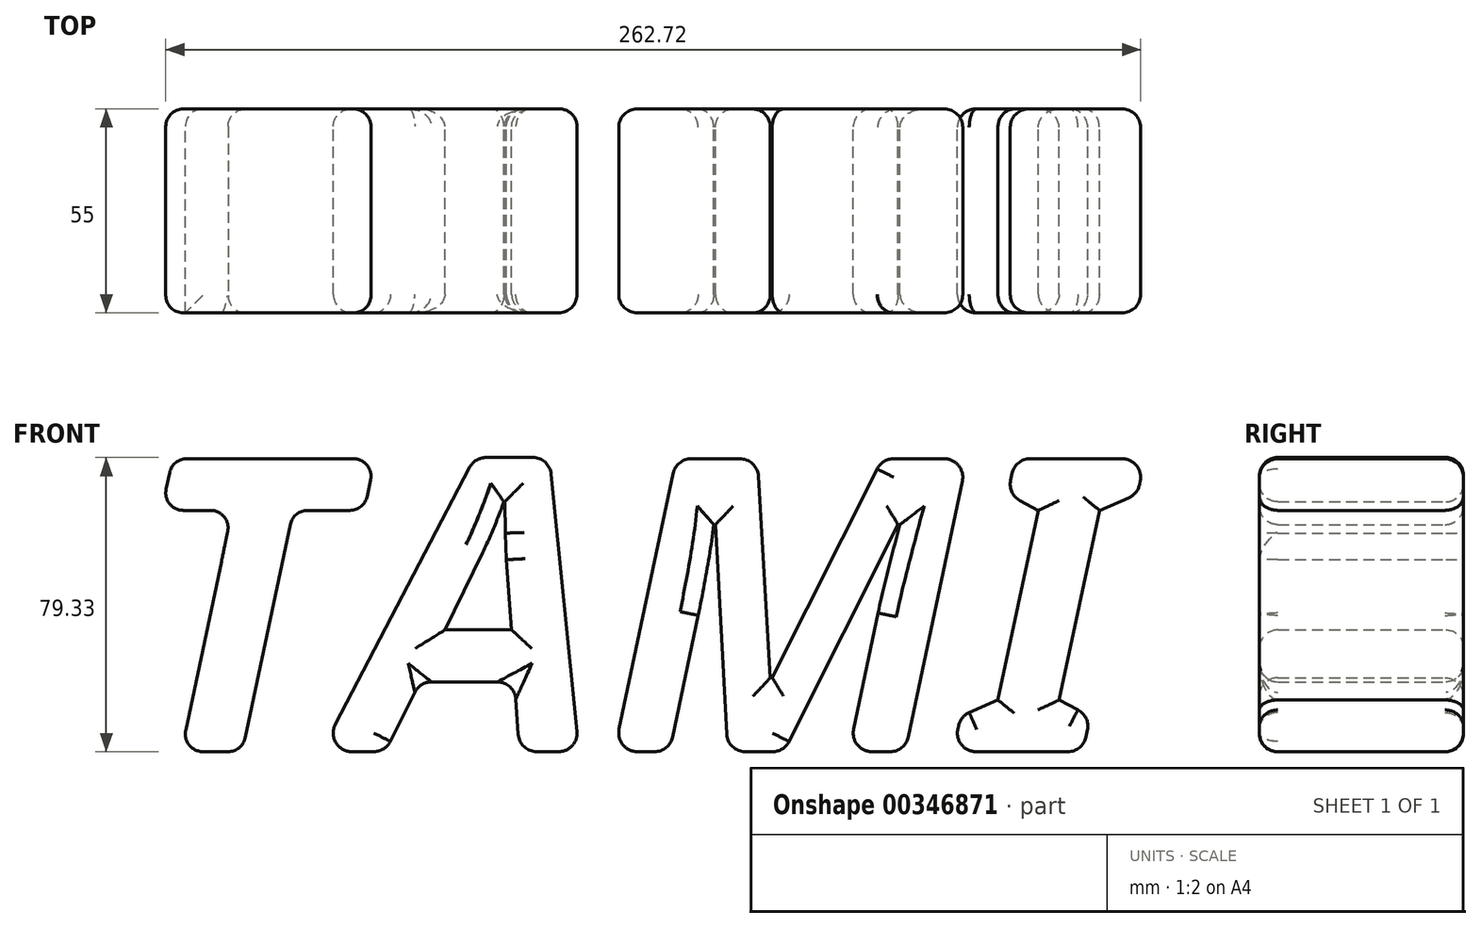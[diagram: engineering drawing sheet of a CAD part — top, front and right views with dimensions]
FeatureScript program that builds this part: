
annotation { "Feature Type Name" : "Feature", "Feature Type Description" : "" }
export const myFeature = defineFeature(function(context is Context, id is Id, definition is map)
    precondition{}
    {
        {
            var Q0;
            Q0=qCreatedBy(makeId("Front.planeOp"),FACE);
            var sketch = newSketch(context, id + "F0", { "sketchPlane" : qUnion([Q0])});
            skText(sketch, "E0", { "text": "TAMI", "fontName": "NotoSans-BoldItalic.ttf"});
            const initialGuessF0  = {"E0": [0, 0, 1, 0, 0.07968]};
            skSetInitialGuess(sketch, initialGuessF0);
            skSolve(sketch);
        }
        {
            var Q0;
            Q0 = qSketchRegion(id + "F0", true);
            extrude(context, id + "F1", {"entities" : qUnion([Q0]), "depth" : 30 * mm, "hasSecondDirection" : true, "secondDirectionOppositeDirection" : true, "secondDirectionDepth" : 25 * mm});
        }
        {
            var Q0;
            Q0=makeQuery(id+"F1.opExtrude","CAP_FACE",FACE,{"disambiguationData":[OSD([sQuery(id+"F0.wireOp",EDGE,"E0.sketch_text.stroke-8"),sQuery(id+"F0.wireOp",EDGE,"E0.sketch_text.stroke-9"),sQuery(id+"F0.wireOp",EDGE,"E0.sketch_text.stroke-10"),sQuery(id+"F0.wireOp",EDGE,"E0.sketch_text.stroke-11"),sQuery(id+"F0.wireOp",EDGE,"E0.sketch_text.stroke-12"),sQuery(id+"F0.wireOp",EDGE,"E0.sketch_text.stroke-13"),sQuery(id+"F0.wireOp",EDGE,"E0.sketch_text.stroke-14"),sQuery(id+"F0.wireOp",EDGE,"E0.sketch_text.stroke-15"),sQuery(id+"F0.wireOp",EDGE,"E0.sketch_text.stroke-16"),sQuery(id+"F0.wireOp",EDGE,"E0.sketch_text.stroke-17"),sQuery(id+"F0.wireOp",EDGE,"E0.sketch_text.stroke-18"),sQuery(id+"F0.wireOp",EDGE,"E0.sketch_text.stroke-19"),sQuery(id+"F0.wireOp",EDGE,"E0.sketch_text.stroke-20"),sQuery(id+"F0.wireOp",EDGE,"E0.sketch_text.stroke-21"),sQuery(id+"F0.wireOp",EDGE,"E0.sketch_text.stroke-22")])],"isStart":true});
            var Q1;
            Q1=makeQuery(id+"F1.opExtrude","CAP_EDGE",EDGE,{"disambiguationData":[OSD([sQuery(id+"F0.wireOp",EDGE,"E0.sketch_text.stroke-4")])],"isStart":true});
            var Q2;
            Q2=makeQuery(id+"F1.opExtrude","CAP_EDGE",EDGE,{"disambiguationData":[OSD([sQuery(id+"F0.wireOp",EDGE,"E0.sketch_text.stroke-7")])],"isStart":true});
            var Q3;
            Q3=makeQuery(id+"F1.opExtrude","CAP_EDGE",EDGE,{"disambiguationData":[OSD([sQuery(id+"F0.wireOp",EDGE,"E0.sketch_text.stroke-0")])],"isStart":true});
            var Q4;
            Q4=makeQuery(id+"F1.opExtrude","CAP_EDGE",EDGE,{"disambiguationData":[OSD([sQuery(id+"F0.wireOp",EDGE,"E0.sketch_text.stroke-6")])],"isStart":true});
            var Q5;
            Q5=makeQuery(id+"F1.opExtrude","CAP_EDGE",EDGE,{"disambiguationData":[OSD([sQuery(id+"F0.wireOp",EDGE,"E0.sketch_text.stroke-5")])],"isStart":true});
            var Q6;
            Q6=makeQuery(id+"F1.opExtrude","SWEPT_EDGE",EDGE,{"disambiguationData":[OSD([sQuery(id+"F0.wireOp",EDGE,"E0.sketch_text.stroke-4"),sQuery(id+"F0.wireOp",EDGE,"E0.sketch_text.stroke-5")])]});
            var Q7;
            Q7=makeQuery(id+"F1.opExtrude","CAP_EDGE",EDGE,{"disambiguationData":[OSD([sQuery(id+"F0.wireOp",EDGE,"E0.sketch_text.stroke-3")])],"isStart":true});
            var Q8;
            Q8=makeQuery(id+"F1.opExtrude","CAP_EDGE",EDGE,{"disambiguationData":[OSD([sQuery(id+"F0.wireOp",EDGE,"E0.sketch_text.stroke-2")])],"isStart":true});
            var Q9;
            Q9=makeQuery(id+"F1.opExtrude","CAP_EDGE",EDGE,{"disambiguationData":[OSD([sQuery(id+"F0.wireOp",EDGE,"E0.sketch_text.stroke-4")])],"isStart":false});
            var Q10;
            Q10=makeQuery(id+"F1.opExtrude","CAP_EDGE",EDGE,{"disambiguationData":[OSD([sQuery(id+"F0.wireOp",EDGE,"E0.sketch_text.stroke-5")])],"isStart":false});
            var Q11;
            Q11=makeQuery(id+"F1.opExtrude","CAP_EDGE",EDGE,{"disambiguationData":[OSD([sQuery(id+"F0.wireOp",EDGE,"E0.sketch_text.stroke-6")])],"isStart":false});
            var Q12;
            Q12=makeQuery(id+"F1.opExtrude","CAP_EDGE",EDGE,{"disambiguationData":[OSD([sQuery(id+"F0.wireOp",EDGE,"E0.sketch_text.stroke-2")])],"isStart":false});
            var Q13;
            Q13=makeQuery(id+"F1.opExtrude","CAP_EDGE",EDGE,{"disambiguationData":[OSD([sQuery(id+"F0.wireOp",EDGE,"E0.sketch_text.stroke-3")])],"isStart":false});
            var Q14;
            Q14=makeQuery(id+"F1.opExtrude","SWEPT_EDGE",EDGE,{"disambiguationData":[OSD([sQuery(id+"F0.wireOp",EDGE,"E0.sketch_text.stroke-3"),sQuery(id+"F0.wireOp",EDGE,"E0.sketch_text.stroke-4")])]});
            var Q15;
            Q15=makeQuery(id+"F1.opExtrude","CAP_EDGE",EDGE,{"disambiguationData":[OSD([sQuery(id+"F0.wireOp",EDGE,"E0.sketch_text.stroke-1")])],"isStart":true});
            var Q16;
            Q16=makeQuery(id+"F1.opExtrude","SWEPT_EDGE",EDGE,{"disambiguationData":[OSD([sQuery(id+"F0.wireOp",EDGE,"E0.sketch_text.stroke-2"),sQuery(id+"F0.wireOp",EDGE,"E0.sketch_text.stroke-3")])]});
            var Q17;
            Q17=makeQuery(id+"F1.opExtrude","SWEPT_EDGE",EDGE,{"disambiguationData":[OSD([sQuery(id+"F0.wireOp",EDGE,"E0.sketch_text.stroke-1"),sQuery(id+"F0.wireOp",EDGE,"E0.sketch_text.stroke-2")])]});
            var Q18;
            Q18=makeQuery(id+"F1.opExtrude","SWEPT_EDGE",EDGE,{"disambiguationData":[OSD([sQuery(id+"F0.wireOp",EDGE,"E0.sketch_text.stroke-0"),sQuery(id+"F0.wireOp",EDGE,"E0.sketch_text.stroke-7")])]});
            var Q19;
            Q19=makeQuery(id+"F1.opExtrude","SWEPT_EDGE",EDGE,{"disambiguationData":[OSD([sQuery(id+"F0.wireOp",EDGE,"E0.sketch_text.stroke-0"),sQuery(id+"F0.wireOp",EDGE,"E0.sketch_text.stroke-1")])]});
            var Q20;
            Q20=makeQuery(id+"F1.opExtrude","CAP_EDGE",EDGE,{"disambiguationData":[OSD([sQuery(id+"F0.wireOp",EDGE,"E0.sketch_text.stroke-0")])],"isStart":false});
            var Q21;
            Q21=makeQuery(id+"F1.opExtrude","CAP_EDGE",EDGE,{"disambiguationData":[OSD([sQuery(id+"F0.wireOp",EDGE,"E0.sketch_text.stroke-7")])],"isStart":false});
            var Q22;
            Q22=makeQuery(id+"F1.opExtrude","SWEPT_FACE",FACE,{"disambiguationData":[OSD([sQuery(id+"F0.wireOp",EDGE,"E0.sketch_text.stroke-6")])]});
            fillet(context, id + "F2", {"entities" : qUnion([Q0, Q1, Q2, Q3, Q4, Q5, Q6, Q7, Q8, Q9, Q10, Q11, Q12, Q13, Q14, Q15, Q16, Q17, Q18, Q19, Q20, Q21, Q22]), "radius" : 4.74 * mm, "tangentPropagation" : true, "allowEdgeOverflow" : false});
        }
        {
            var Q0;
            Q0=makeQuery(id+"F1.opExtrude","SWEPT_EDGE",EDGE,{"disambiguationData":[OSD([sQuery(id+"F0.wireOp",EDGE,"E0.sketch_text.stroke-12"),sQuery(id+"F0.wireOp",EDGE,"E0.sketch_text.stroke-13")])]});
            var Q1;
            Q1=makeQuery(id+"F1.opExtrude","SWEPT_FACE",FACE,{"disambiguationData":[OSD([sQuery(id+"F0.wireOp",EDGE,"E0.sketch_text.stroke-12")])]});
            var Q2;
            Q2=makeQuery(id+"F1.opExtrude","SWEPT_FACE",FACE,{"disambiguationData":[OSD([sQuery(id+"F0.wireOp",EDGE,"E0.sketch_text.stroke-11")])]});
            var Q3;
            Q3=makeQuery(id+"F1.opExtrude","CAP_EDGE",EDGE,{"disambiguationData":[OSD([sQuery(id+"F0.wireOp",EDGE,"E0.sketch_text.stroke-16")])],"isStart":false});
            var Q4;
            Q4=makeQuery(id+"F1.opExtrude","CAP_FACE",FACE,{"disambiguationData":[OSD([sQuery(id+"F0.wireOp",EDGE,"E0.sketch_text.stroke-8"),sQuery(id+"F0.wireOp",EDGE,"E0.sketch_text.stroke-9"),sQuery(id+"F0.wireOp",EDGE,"E0.sketch_text.stroke-10"),sQuery(id+"F0.wireOp",EDGE,"E0.sketch_text.stroke-11"),sQuery(id+"F0.wireOp",EDGE,"E0.sketch_text.stroke-12"),sQuery(id+"F0.wireOp",EDGE,"E0.sketch_text.stroke-13"),sQuery(id+"F0.wireOp",EDGE,"E0.sketch_text.stroke-14"),sQuery(id+"F0.wireOp",EDGE,"E0.sketch_text.stroke-15"),sQuery(id+"F0.wireOp",EDGE,"E0.sketch_text.stroke-16"),sQuery(id+"F0.wireOp",EDGE,"E0.sketch_text.stroke-17"),sQuery(id+"F0.wireOp",EDGE,"E0.sketch_text.stroke-18"),sQuery(id+"F0.wireOp",EDGE,"E0.sketch_text.stroke-19"),sQuery(id+"F0.wireOp",EDGE,"E0.sketch_text.stroke-20"),sQuery(id+"F0.wireOp",EDGE,"E0.sketch_text.stroke-21"),sQuery(id+"F0.wireOp",EDGE,"E0.sketch_text.stroke-22")])],"isStart":false});
            var Q5;
            Q5=makeQuery(id+"F1.opExtrude","SWEPT_FACE",FACE,{"disambiguationData":[OSD([sQuery(id+"F0.wireOp",EDGE,"E0.sketch_text.stroke-13")])]});
            fillet(context, id + "F3", {"entities" : qUnion([Q0, Q1, Q2, Q3, Q4, Q5]), "radius" : 5 * mm, "tangentPropagation" : true, "allowEdgeOverflow" : false});
        }
        {
            var Q0;
            Q0=makeQuery(id+"F1.opExtrude","SWEPT_EDGE",EDGE,{"disambiguationData":[OSD([sQuery(id+"F0.wireOp",EDGE,"E0.sketch_text.stroke-8"),sQuery(id+"F0.wireOp",EDGE,"E0.sketch_text.stroke-15")])]});
            var Q1;
            Q1=makeQuery(id+"F1.opExtrude","SWEPT_FACE",FACE,{"disambiguationData":[OSD([sQuery(id+"F0.wireOp",EDGE,"E0.sketch_text.stroke-14")])]});
            var Q2;
            Q2=makeQuery(id+"F1.opExtrude","SWEPT_EDGE",EDGE,{"disambiguationData":[OSD([sQuery(id+"F0.wireOp",EDGE,"E0.sketch_text.stroke-8"),sQuery(id+"F0.wireOp",EDGE,"E0.sketch_text.stroke-9")])]});
            var Q3;
            Q3=makeQuery(id+"F1.opExtrude","SWEPT_EDGE",EDGE,{"disambiguationData":[OSD([sQuery(id+"F0.wireOp",EDGE,"E0.sketch_text.stroke-9"),sQuery(id+"F0.wireOp",EDGE,"E0.sketch_text.stroke-10")])]});
            var Q4;
            Q4=makeQuery(id+"F1.opExtrude","SWEPT_FACE",FACE,{"disambiguationData":[OSD([sQuery(id+"F0.wireOp",EDGE,"E0.sketch_text.stroke-36")])]});
            var Q5;
            Q5=makeQuery(id+"F1.opExtrude","CAP_FACE",FACE,{"disambiguationData":[OSD([sQuery(id+"F0.wireOp",EDGE,"E0.sketch_text.stroke-23"),sQuery(id+"F0.wireOp",EDGE,"E0.sketch_text.stroke-24"),sQuery(id+"F0.wireOp",EDGE,"E0.sketch_text.stroke-25"),sQuery(id+"F0.wireOp",EDGE,"E0.sketch_text.stroke-26"),sQuery(id+"F0.wireOp",EDGE,"E0.sketch_text.stroke-27"),sQuery(id+"F0.wireOp",EDGE,"E0.sketch_text.stroke-28"),sQuery(id+"F0.wireOp",EDGE,"E0.sketch_text.stroke-29"),sQuery(id+"F0.wireOp",EDGE,"E0.sketch_text.stroke-30"),sQuery(id+"F0.wireOp",EDGE,"E0.sketch_text.stroke-31"),sQuery(id+"F0.wireOp",EDGE,"E0.sketch_text.stroke-32"),sQuery(id+"F0.wireOp",EDGE,"E0.sketch_text.stroke-33"),sQuery(id+"F0.wireOp",EDGE,"E0.sketch_text.stroke-34"),sQuery(id+"F0.wireOp",EDGE,"E0.sketch_text.stroke-35"),sQuery(id+"F0.wireOp",EDGE,"E0.sketch_text.stroke-36"),sQuery(id+"F0.wireOp",EDGE,"E0.sketch_text.stroke-37"),sQuery(id+"F0.wireOp",EDGE,"E0.sketch_text.stroke-38"),sQuery(id+"F0.wireOp",EDGE,"E0.sketch_text.stroke-39"),sQuery(id+"F0.wireOp",EDGE,"E0.sketch_text.stroke-40")])],"isStart":false});
            fillet(context, id + "F4", {"entities" : qUnion([Q0, Q1, Q2, Q3, Q4, Q5]), "radius" : 5 * mm, "tangentPropagation" : true, "allowEdgeOverflow" : false});
        }
        {
            var Q0;
            Q0=makeQuery(id+"F1.opExtrude","CAP_FACE",FACE,{"disambiguationData":[OSD([sQuery(id+"F0.wireOp",EDGE,"E0.sketch_text.stroke-23"),sQuery(id+"F0.wireOp",EDGE,"E0.sketch_text.stroke-24"),sQuery(id+"F0.wireOp",EDGE,"E0.sketch_text.stroke-25"),sQuery(id+"F0.wireOp",EDGE,"E0.sketch_text.stroke-26"),sQuery(id+"F0.wireOp",EDGE,"E0.sketch_text.stroke-27"),sQuery(id+"F0.wireOp",EDGE,"E0.sketch_text.stroke-28"),sQuery(id+"F0.wireOp",EDGE,"E0.sketch_text.stroke-29"),sQuery(id+"F0.wireOp",EDGE,"E0.sketch_text.stroke-30"),sQuery(id+"F0.wireOp",EDGE,"E0.sketch_text.stroke-31"),sQuery(id+"F0.wireOp",EDGE,"E0.sketch_text.stroke-32"),sQuery(id+"F0.wireOp",EDGE,"E0.sketch_text.stroke-33"),sQuery(id+"F0.wireOp",EDGE,"E0.sketch_text.stroke-34"),sQuery(id+"F0.wireOp",EDGE,"E0.sketch_text.stroke-35"),sQuery(id+"F0.wireOp",EDGE,"E0.sketch_text.stroke-36"),sQuery(id+"F0.wireOp",EDGE,"E0.sketch_text.stroke-37"),sQuery(id+"F0.wireOp",EDGE,"E0.sketch_text.stroke-38"),sQuery(id+"F0.wireOp",EDGE,"E0.sketch_text.stroke-39"),sQuery(id+"F0.wireOp",EDGE,"E0.sketch_text.stroke-40")])],"isStart":true});
            var Q1;
            Q1=makeQuery(id+"F1.opExtrude","SWEPT_FACE",FACE,{"disambiguationData":[OSD([sQuery(id+"F0.wireOp",EDGE,"E0.sketch_text.stroke-38")])]});
            var Q2;
            Q2=makeQuery(id+"F1.opExtrude","SWEPT_FACE",FACE,{"disambiguationData":[OSD([sQuery(id+"F0.wireOp",EDGE,"E0.sketch_text.stroke-24")])]});
            var Q3;
            Q3=makeQuery(id+"F1.opExtrude","SWEPT_EDGE",EDGE,{"disambiguationData":[OSD([sQuery(id+"F0.wireOp",EDGE,"E0.sketch_text.stroke-26"),sQuery(id+"F0.wireOp",EDGE,"E0.sketch_text.stroke-27")])]});
            var Q4;
            Q4=makeQuery(id+"F1.opExtrude","SWEPT_EDGE",EDGE,{"disambiguationData":[OSD([sQuery(id+"F0.wireOp",EDGE,"E0.sketch_text.stroke-31"),sQuery(id+"F0.wireOp",EDGE,"E0.sketch_text.stroke-32")])]});
            var Q5;
            Q5=makeQuery(id+"F1.opExtrude","SWEPT_EDGE",EDGE,{"disambiguationData":[OSD([sQuery(id+"F0.wireOp",EDGE,"E0.sketch_text.stroke-30"),sQuery(id+"F0.wireOp",EDGE,"E0.sketch_text.stroke-31")])]});
            fillet(context, id + "F5", {"entities" : qUnion([Q0, Q1, Q2, Q3, Q4, Q5]), "radius" : 5 * mm, "tangentPropagation" : true, "allowEdgeOverflow" : false});
        }
        {
            var Q0;
            Q0=makeQuery(id+"F1.opExtrude","SWEPT_EDGE",EDGE,{"disambiguationData":[OSD([sQuery(id+"F0.wireOp",EDGE,"E0.sketch_text.stroke-25"),sQuery(id+"F0.wireOp",EDGE,"E0.sketch_text.stroke-26")])]});
            fillet(context, id + "F6", {"entities" : qUnion([Q0]), "radius" : 5 * mm, "tangentPropagation" : true, "allowEdgeOverflow" : false});
        }
        {
            var Q0;
            Q0=makeQuery(id+"F1.opExtrude","CAP_EDGE",EDGE,{"disambiguationData":[OSD([sQuery(id+"F0.wireOp",EDGE,"E0.sketch_text.stroke-47")])],"isStart":true});
            var Q1;
            Q1=makeQuery(id+"F1.opExtrude","CAP_EDGE",EDGE,{"disambiguationData":[OSD([sQuery(id+"F0.wireOp",EDGE,"E0.sketch_text.stroke-50")])],"isStart":false});
            var Q2;
            Q2=makeQuery(id+"F1.opExtrude","CAP_FACE",FACE,{"disambiguationData":[OSD([sQuery(id+"F0.wireOp",EDGE,"E0.sketch_text.stroke-41"),sQuery(id+"F0.wireOp",EDGE,"E0.sketch_text.stroke-42"),sQuery(id+"F0.wireOp",EDGE,"E0.sketch_text.stroke-43"),sQuery(id+"F0.wireOp",EDGE,"E0.sketch_text.stroke-44"),sQuery(id+"F0.wireOp",EDGE,"E0.sketch_text.stroke-45"),sQuery(id+"F0.wireOp",EDGE,"E0.sketch_text.stroke-46"),sQuery(id+"F0.wireOp",EDGE,"E0.sketch_text.stroke-47"),sQuery(id+"F0.wireOp",EDGE,"E0.sketch_text.stroke-48"),sQuery(id+"F0.wireOp",EDGE,"E0.sketch_text.stroke-49"),sQuery(id+"F0.wireOp",EDGE,"E0.sketch_text.stroke-50"),sQuery(id+"F0.wireOp",EDGE,"E0.sketch_text.stroke-51"),sQuery(id+"F0.wireOp",EDGE,"E0.sketch_text.stroke-52")])],"isStart":false});
            var Q3;
            Q3=makeQuery(id+"F1.opExtrude","SWEPT_FACE",FACE,{"disambiguationData":[OSD([sQuery(id+"F0.wireOp",EDGE,"E0.sketch_text.stroke-47")])]});
            var Q4;
            Q4=makeQuery(id+"F1.opExtrude","SWEPT_FACE",FACE,{"disambiguationData":[OSD([sQuery(id+"F0.wireOp",EDGE,"E0.sketch_text.stroke-41")])]});
            var Q5;
            Q5=makeQuery(id+"F1.opExtrude","CAP_FACE",FACE,{"disambiguationData":[OSD([sQuery(id+"F0.wireOp",EDGE,"E0.sketch_text.stroke-41"),sQuery(id+"F0.wireOp",EDGE,"E0.sketch_text.stroke-42"),sQuery(id+"F0.wireOp",EDGE,"E0.sketch_text.stroke-43"),sQuery(id+"F0.wireOp",EDGE,"E0.sketch_text.stroke-44"),sQuery(id+"F0.wireOp",EDGE,"E0.sketch_text.stroke-45"),sQuery(id+"F0.wireOp",EDGE,"E0.sketch_text.stroke-46"),sQuery(id+"F0.wireOp",EDGE,"E0.sketch_text.stroke-47"),sQuery(id+"F0.wireOp",EDGE,"E0.sketch_text.stroke-48"),sQuery(id+"F0.wireOp",EDGE,"E0.sketch_text.stroke-49"),sQuery(id+"F0.wireOp",EDGE,"E0.sketch_text.stroke-50"),sQuery(id+"F0.wireOp",EDGE,"E0.sketch_text.stroke-51"),sQuery(id+"F0.wireOp",EDGE,"E0.sketch_text.stroke-52")])],"isStart":true});
            var Q6;
            Q6=makeQuery(id+"F1.opExtrude","SWEPT_EDGE",EDGE,{"disambiguationData":[OSD([sQuery(id+"F0.wireOp",EDGE,"E0.sketch_text.stroke-45"),sQuery(id+"F0.wireOp",EDGE,"E0.sketch_text.stroke-46")])]});
            var Q7;
            Q7=makeQuery(id+"F1.opExtrude","SWEPT_EDGE",EDGE,{"disambiguationData":[OSD([sQuery(id+"F0.wireOp",EDGE,"E0.sketch_text.stroke-48"),sQuery(id+"F0.wireOp",EDGE,"E0.sketch_text.stroke-49")])]});
            fillet(context, id + "F7", {"entities" : qUnion([Q0, Q1, Q2, Q3, Q4, Q5, Q6, Q7]), "radius" : 5 * mm, "tangentPropagation" : true, "allowEdgeOverflow" : false});
        }
        {
            var Q0;
            Q0=makeQuery(id+"F1.opExtrude","SWEPT_EDGE",EDGE,{"disambiguationData":[OSD([sQuery(id+"F0.wireOp",EDGE,"E0.sketch_text.stroke-51"),sQuery(id+"F0.wireOp",EDGE,"E0.sketch_text.stroke-52")])]});
            fillet(context, id + "F8", {"entities" : qUnion([Q0]), "radius" : 5 * mm, "tangentPropagation" : true, "allowEdgeOverflow" : false});
        }
        {
            var Q0;
            Q0=makeQuery(id+"F1.opExtrude","SWEPT_EDGE",EDGE,{"disambiguationData":[OSD([sQuery(id+"F0.wireOp",EDGE,"E0.sketch_text.stroke-42"),sQuery(id+"F0.wireOp",EDGE,"E0.sketch_text.stroke-43")])]});
            fillet(context, id + "F9", {"entities" : qUnion([Q0]), "radius" : 5 * mm, "tangentPropagation" : true, "allowEdgeOverflow" : false});
        }
    });
